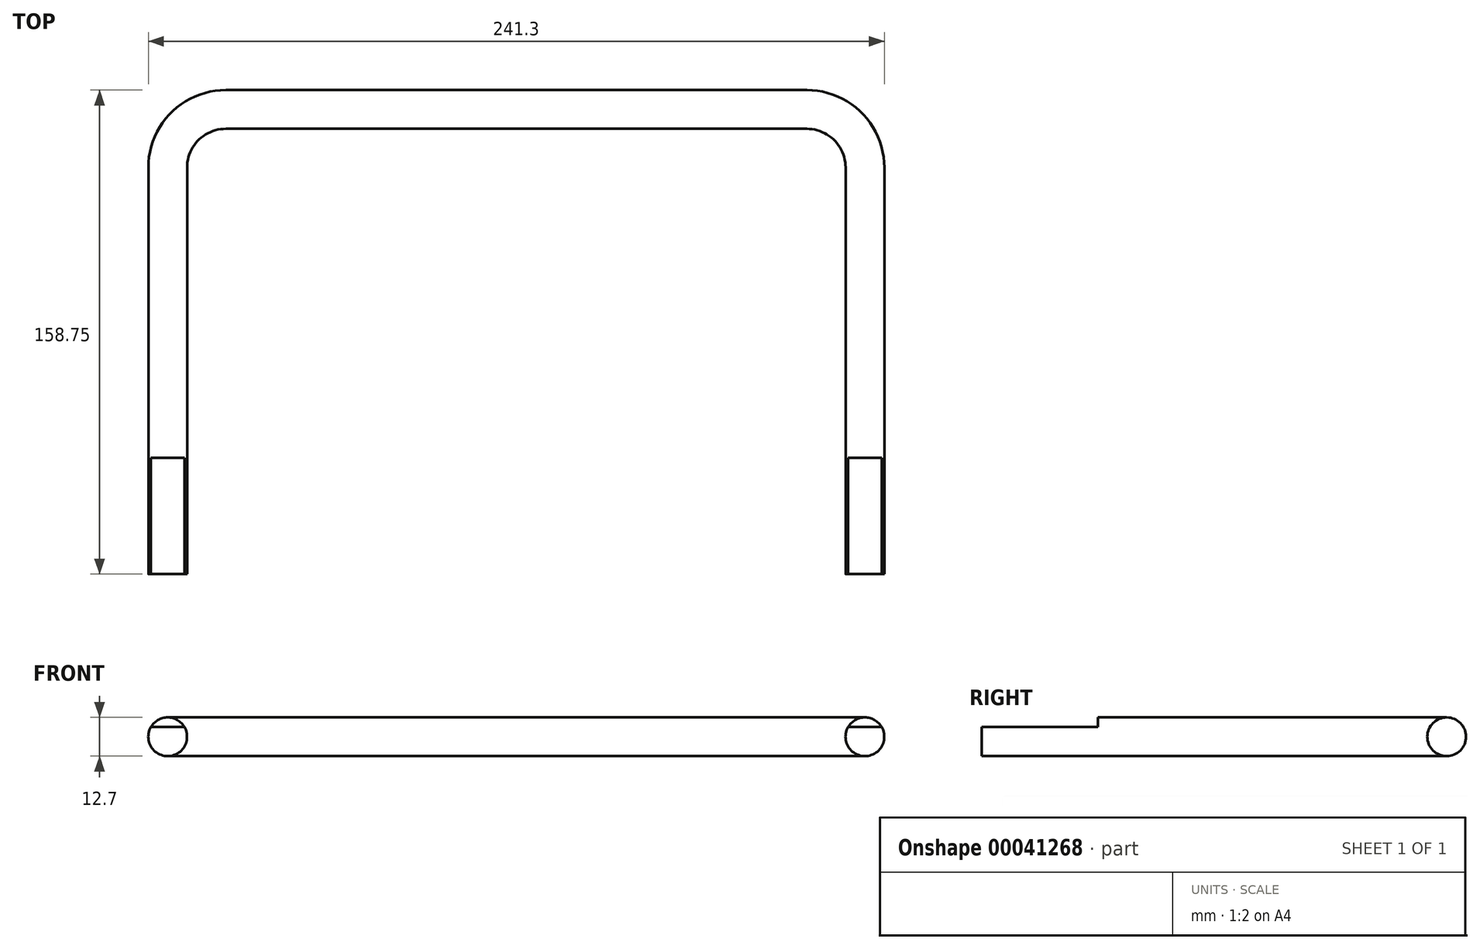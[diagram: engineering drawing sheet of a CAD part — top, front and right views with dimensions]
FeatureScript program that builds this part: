
annotation { "Feature Type Name" : "Feature", "Feature Type Description" : "" }
export const myFeature = defineFeature(function(context is Context, id is Id, definition is map)
    precondition{}
    {
        {
            var Q0;
            Q0=qCreatedBy(makeId("Front.planeOp"),FACE);
            var sketch = newSketch(context, id + "F0", { "sketchPlane" : qUnion([Q0])});
            skLineSegment(sketch, "E0", {"start": v(0, 0) * mm, "end": v(0, 43.3) * mm, "construction": true});
            skCircle(sketch, "E1", {"center": v(19.05, 0) * mm, "radius": 6.35 * mm});
            skSolve(sketch);
        }
        {
            var Q0;
            Q0=makeQuery(id+"F0.imprint","IMPRINT",FACE,{"disambiguationData":[TD([[makeQuery(id+"F0.imprint","IMPRINT",EDGE,{"derivedFrom":sQuery(id+"F0.wireOp",EDGE,"E1")}),1.0]])]});
            var Q1;
            Q1=sQuery(id+"F0.wireOp",EDGE,"E0");
            revolve(context, id + "F1", {"entities" : qUnion([Q0]), "axis" : qUnion([Q1]), "revolveType" : RevolveType.ONE_DIRECTION, "angle" : 90 * degree});
        }
        {
            var Q0;
            Q0=qCreatedBy(makeId("Front.planeOp"),FACE);
            var sketch = newSketch(context, id + "F2", { "sketchPlane" : qUnion([Q0])});
            skLineSegment(sketch, "E2", {"start": v(0, 0) * mm, "end": v(-190.5, 0) * mm, "construction": true});
            skCircle(sketch, "E3", {"center": v(-209.55, 0) * mm, "radius": 6.35 * mm});
            skLineSegment(sketch, "E4", {"start": v(-190.5, 0) * mm, "end": v(-190.5, 61.43) * mm, "construction": true});
            skSolve(sketch);
        }
        {
            var Q0;
            Q0=makeQuery(id+"F2.imprint","IMPRINT",FACE,{"disambiguationData":[TD([[makeQuery(id+"F2.imprint","IMPRINT",EDGE,{"derivedFrom":sQuery(id+"F2.wireOp",EDGE,"E3")}),1.0]])]});
            var Q1;
            Q1=sQuery(id+"F2.wireOp",EDGE,"E4");
            revolve(context, id + "F3", {"entities" : qUnion([Q0]), "axis" : qUnion([Q1]), "revolveType" : RevolveType.ONE_DIRECTION, "oppositeDirection" : true, "angle" : 90 * degree});
        }
        {
            var Q0;
            Q0=makeQuery(id+"F1.opRevolve","CAP_FACE",FACE,{"disambiguationData":[OSD([sQuery(id+"F0.wireOp",EDGE,"E1")])],"isStart":false});
            extrude(context, id + "F4", {"entities" : qUnion([Q0]), "operationType" : NewBodyOperationType.ADD, "endBound" : BoundingType.UP_TO_NEXT, "depth" : 25.4 * mm});
        }
        {
            var Q0;
            Q0=makeQuery(id+"F1.opRevolve","CAP_FACE",FACE,{"disambiguationData":[OSD([sQuery(id+"F0.wireOp",EDGE,"E1")])],"isStart":true});
            extrude(context, id + "F5", {"entities" : qUnion([Q0]), "operationType" : NewBodyOperationType.ADD, "depth" : 133.35 * mm});
        }
        {
            var Q0;
            Q0=makeQuery(id+"F3.opRevolve","CAP_FACE",FACE,{"disambiguationData":[OSD([sQuery(id+"F2.wireOp",EDGE,"E3")])],"isStart":true});
            extrude(context, id + "F6", {"entities" : qUnion([Q0]), "operationType" : NewBodyOperationType.ADD, "depth" : 133.35 * mm});
        }
        {
            var Q0;
            Q0=makeQuery(id+"F6.opExtrude","CAP_FACE",FACE,{"disambiguationData":[OSD([sQuery(id+"F2.wireOp",EDGE,"E3")])],"isStart":false});
            var sketch = newSketch(context, id + "F7", { "sketchPlane" : qUnion([Q0])});
            skLineSegment(sketch, "E5.bottom", {"start": v(-229.96, 34.12) * mm, "end": v(33.05, 34.12) * mm});
            skLineSegment(sketch, "E5.top", {"start": v(-229.96, 3.18) * mm, "end": v(33.05, 3.18) * mm});
            skLineSegment(sketch, "E5.left", {"start": v(-229.96, 34.12) * mm, "end": v(-229.96, 3.18) * mm});
            skLineSegment(sketch, "E5.right", {"start": v(33.05, 34.12) * mm, "end": v(33.05, 3.18) * mm});
            skSolve(sketch);
        }
        {
            var Q0;
            Q0=makeQuery(id+"F7.imprint","IMPRINT",FACE,{"disambiguationData":[TD([[makeQuery(id+"F7.imprint","IMPRINT",EDGE,{"derivedFrom":sQuery(id+"F7.wireOp",EDGE,"E5.bottom")}),-1.0]])]});
            extrude(context, id + "F8", {"entities" : qUnion([Q0]), "operationType" : NewBodyOperationType.REMOVE, "oppositeDirection" : true, "depth" : 38.1 * mm});
        }
        {
            var Q0;
            Q0=makeQuery(id+"F6.opExtrude","CAP_FACE",FACE,{"disambiguationData":[OSD([sQuery(id+"F2.wireOp",EDGE,"E3")])],"isStart":false});
            cPlane(context, id + "F9", {"entities" : qUnion([Q0]), "cplaneType" : CPlaneType.OFFSET, "offset" : 3.17 * mm, "width" : 152.4 * mm, "height" : 152.4 * mm});
        }
        {
            var Q0;
            Q0=qCreatedBy(id+"F9.planeOp",FACE);
            var sketch = newSketch(context, id + "F10", { "sketchPlane" : qUnion([Q0])});
            skLineSegment(sketch, "E6", {"start": v(-196.55, 0) * mm, "end": v(-228.88, 0) * mm, "construction": true});
            skSolve(sketch);
        }
        {
            var Q0;
            Q0=qCreatedBy(id+"F9.planeOp",FACE);
            var sketch = newSketch(context, id + "F11", { "sketchPlane" : qUnion([Q0])});
            skLineSegment(sketch, "E7.bottom", {"start": v(-223.82, 17.81) * mm, "end": v(-196.95, 17.81) * mm});
            skLineSegment(sketch, "E7.top", {"start": v(-223.82, 3.17) * mm, "end": v(-196.95, 3.18) * mm});
            skLineSegment(sketch, "E7.left", {"start": v(-223.82, 17.81) * mm, "end": v(-223.82, 3.17) * mm});
            skLineSegment(sketch, "E7.right", {"start": v(-196.95, 17.81) * mm, "end": v(-196.95, 3.18) * mm});
            skSolve(sketch);
        }
        {
            var Q0;
            Q0=makeQuery(id+"F11.imprint","IMPRINT",FACE,{"disambiguationData":[TD([[makeQuery(id+"F11.imprint","IMPRINT",EDGE,{"derivedFrom":sQuery(id+"F11.wireOp",EDGE,"E7.bottom")}),-1.0]])]});
            extrude(context, id + "F12", {"entities" : qUnion([Q0]), "operationType" : NewBodyOperationType.REMOVE, "oppositeDirection" : true, "depth" : 41.27 * mm});
        }
    });
